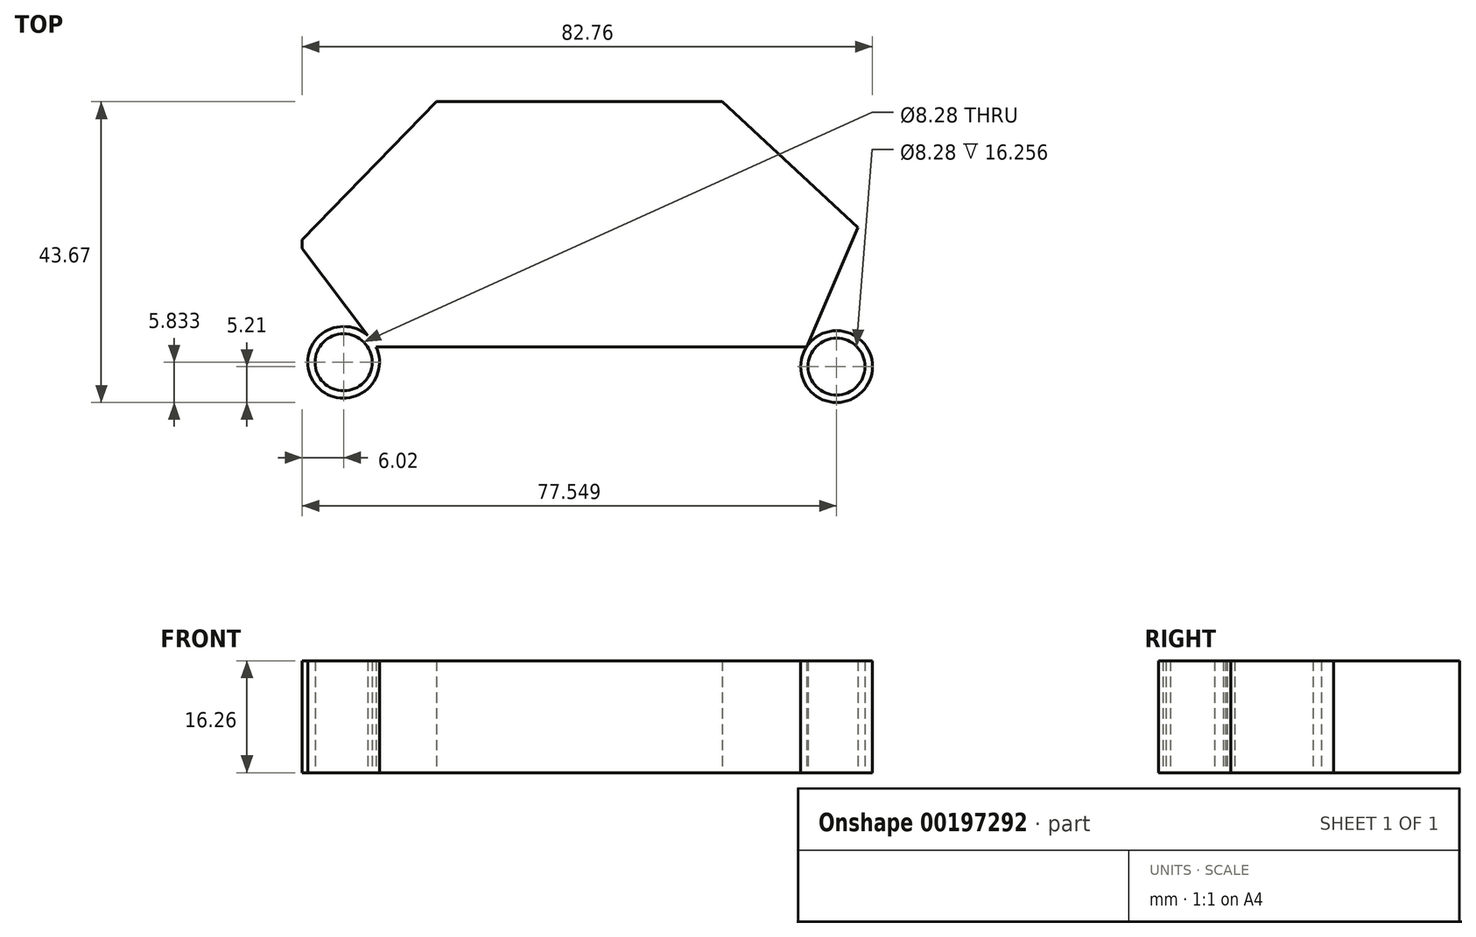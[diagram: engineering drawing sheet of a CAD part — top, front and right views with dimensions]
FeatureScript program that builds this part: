
annotation { "Feature Type Name" : "Feature", "Feature Type Description" : "" }
export const myFeature = defineFeature(function(context is Context, id is Id, definition is map)
    precondition{}
    {
        {
            var Q0;
            Q0=qCreatedBy(makeId("Top.planeOp"),FACE);
            var sketch = newSketch(context, id + "F0", { "sketchPlane" : qUnion([Q0])});
            skLineSegment(sketch, "E0", {"start": v(-35.16, 17.38) * mm, "end": v(-15.66, 37.43) * mm});
            skLineSegment(sketch, "E1", {"start": v(-15.66, 37.43) * mm, "end": v(25.82, 37.43) * mm});
            skLineSegment(sketch, "E2", {"start": v(25.82, 37.43) * mm, "end": v(45.46, 19.16) * mm});
            skLineSegment(sketch, "E3", {"start": v(45.46, 19.16) * mm, "end": v(38.05, 1.85) * mm});
            skLineSegment(sketch, "E4", {"start": v(38.05, 1.85) * mm, "end": v(-24.45, 1.85) * mm});
            skLineSegment(sketch, "E5", {"start": v(-24.45, 1.85) * mm, "end": v(-35.16, 16.14) * mm});
            skLineSegment(sketch, "E6", {"start": v(-35.16, 16.14) * mm, "end": v(-35.16, 17.38) * mm});
            skCircle(sketch, "E7", {"center": v(-29.14, -0.4) * mm, "radius": 5.2 * mm});
            skPoint(sketch, "E7.first.point", {"position": v(-25.56, -4.2) * mm});
            skPoint(sketch, "E7.third.point", {"position": v(-34.16, -1.8) * mm});
            skCircle(sketch, "E8", {"center": v(42.39, -1.03) * mm, "radius": 5.21 * mm});
            skPoint(sketch, "E8.second.point", {"position": v(46.43, -4.33) * mm});
            skPoint(sketch, "E8.third.point", {"position": v(38.05, -3.91) * mm});
            skCircle(sketch, "E9", {"center": v(-29.14, -0.4) * mm, "radius": 4.14 * mm});
            skCircle(sketch, "E10", {"center": v(42.39, -1.03) * mm, "radius": 4.14 * mm});
            skSolve(sketch);
        }
        {
            var Q0;
            Q0 = qSketchRegion(id + "F0", true);
            extrude(context, id + "F1", {"entities" : qUnion([Q0]), "depth" : 16.26 * mm});
        }
    });
